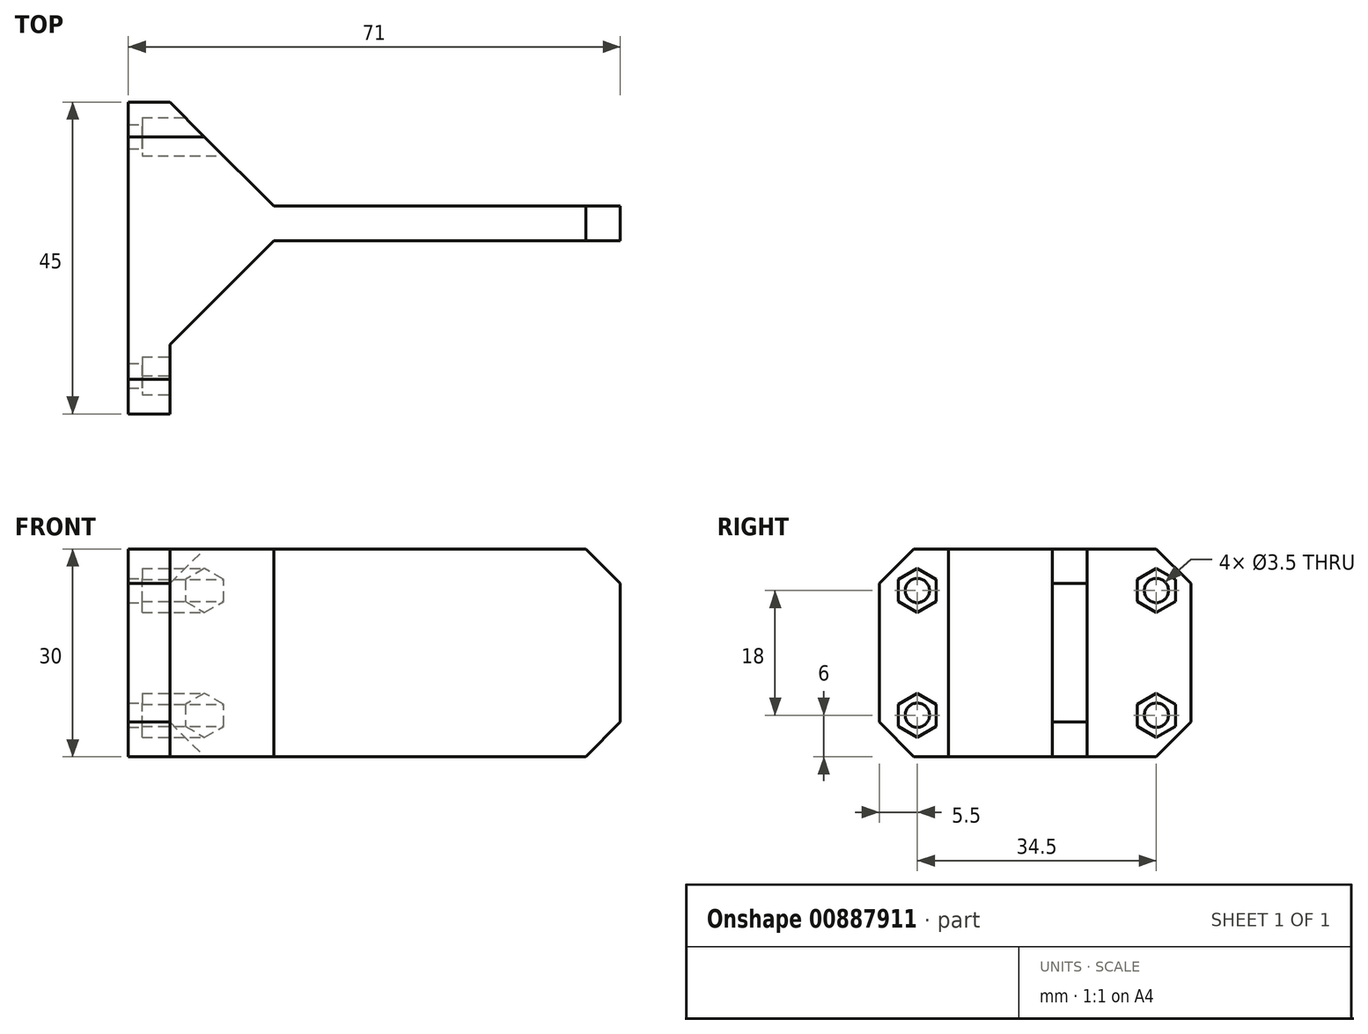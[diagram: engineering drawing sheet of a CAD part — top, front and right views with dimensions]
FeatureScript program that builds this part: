
annotation { "Feature Type Name" : "Feature", "Feature Type Description" : "" }
export const myFeature = defineFeature(function(context is Context, id is Id, definition is map)
    precondition{}
    {
        {
            var Q0;
            Q0=qCreatedBy(makeId("Top.planeOp"),FACE);
            var sketch = newSketch(context, id + "F0", { "sketchPlane" : qUnion([Q0])});
            skLineSegment(sketch, "E0.bottom", {"start": v(0, 0) * mm, "end": v(-6, 0) * mm});
            skLineSegment(sketch, "E0.top", {"start": v(0, 20) * mm, "end": v(-6, 20) * mm});
            skLineSegment(sketch, "E0.left", {"start": v(0, 0) * mm, "end": v(0, 20) * mm});
            skLineSegment(sketch, "E0.right", {"start": v(-6, 0) * mm, "end": v(-6, 20) * mm});
            skLineSegment(sketch, "E1.bottom", {"start": v(0, 0) * mm, "end": v(65, 0) * mm});
            skLineSegment(sketch, "E1.top", {"start": v(0, 5) * mm, "end": v(65, 5) * mm});
            skLineSegment(sketch, "E1.left", {"start": v(0, 0) * mm, "end": v(0, 5) * mm});
            skLineSegment(sketch, "E1.right", {"start": v(65, 0) * mm, "end": v(65, 5) * mm});
            skLineSegment(sketch, "E2.top", {"start": v(0, -25) * mm, "end": v(-6, -25) * mm});
            skLineSegment(sketch, "E2.left", {"start": v(0, 0) * mm, "end": v(0, -25) * mm});
            skLineSegment(sketch, "E2.right", {"start": v(-6, 0) * mm, "end": v(-6, -25) * mm});
            skSolve(sketch);
        }
        {
            var Q0;
            Q0=makeQuery(id+"F0.imprint","IMPRINT",FACE,{"disambiguationData":[TD([[makeQuery(id+"F0.imprint","IMPRINT",EDGE,{"derivedFrom":sQuery(id+"F0.wireOp",EDGE,"E0.bottom")}),-1.0]])]});
            var Q1;
            {var subQ0=sQuery(id+"F0.wireOp",EDGE,"E1.bottom");Q1=makeQuery(id+"F0.imprint","IMPRINT",FACE,{"disambiguationData":[TD([[makeQuery(id+"F0.imprint","IMPRINT",EDGE,{"derivedFrom":subQ0}),1.0]])]});}
            var Q2;
            {var subQ1=sQuery(id+"F0.wireOp",EDGE,"E0.bottom");Q2=makeQuery(id+"F0.imprint","IMPRINT",FACE,{"disambiguationData":[TD([[makeQuery(id+"F0.imprint","IMPRINT",EDGE,{"derivedFrom":subQ1}),-1.0]])]});}
            var Q3;
            Q3=makeQuery(id+"F0.imprint","IMPRINT",FACE,{"disambiguationData":[TD([[makeQuery(id+"F0.imprint","IMPRINT",EDGE,{"derivedFrom":sQuery(id+"F0.wireOp",EDGE,"E0.bottom")}),1.0]])]});
            extrude(context, id + "F1", {"entities" : qUnion([Q0, Q1, Q2, Q3]), "depth" : 30 * mm, "offsetDistance" : 25 * mm});
        }
        {
            var Q0;
            Q0=makeQuery(id+"F1.opExtrude","SWEPT_FACE",FACE,{"disambiguationData":[OSD([sQuery(id+"F0.wireOp",EDGE,"E0.left")])]});
            var sketch = newSketch(context, id + "F2", { "sketchPlane" : qUnion([Q0])});
            skCircle(sketch, "E3.cCircle", {"center": v(15, 24) * mm, "radius": 2.75 * mm, "construction": true});
            skLineSegment(sketch, "E3.0", {"start": v(12.25, 22.41) * mm, "end": v(12.25, 25.59) * mm});
            skLineSegment(sketch, "E3.1", {"start": v(12.25, 25.59) * mm, "end": v(15, 27.18) * mm});
            skLineSegment(sketch, "E3.2", {"start": v(15, 27.18) * mm, "end": v(17.75, 25.59) * mm});
            skLineSegment(sketch, "E3.3", {"start": v(17.75, 25.59) * mm, "end": v(17.75, 22.41) * mm});
            skLineSegment(sketch, "E3.4", {"start": v(17.75, 22.41) * mm, "end": v(15, 20.82) * mm});
            skLineSegment(sketch, "E3.5", {"start": v(15, 20.82) * mm, "end": v(12.25, 22.41) * mm});
            skPoint(sketch, "E3.0.midPoint", {"position": v(12.25, 24) * mm});
            skCircle(sketch, "E4.cCircle", {"center": v(15, 6) * mm, "radius": 2.75 * mm, "construction": true});
            skLineSegment(sketch, "E4.0", {"start": v(12.25, 4.41) * mm, "end": v(12.25, 7.59) * mm});
            skLineSegment(sketch, "E4.1", {"start": v(12.25, 7.59) * mm, "end": v(15, 9.18) * mm});
            skLineSegment(sketch, "E4.2", {"start": v(15, 9.18) * mm, "end": v(17.75, 7.59) * mm});
            skLineSegment(sketch, "E4.3", {"start": v(17.75, 7.59) * mm, "end": v(17.75, 4.41) * mm});
            skLineSegment(sketch, "E4.4", {"start": v(17.75, 4.41) * mm, "end": v(15, 2.82) * mm});
            skLineSegment(sketch, "E4.5", {"start": v(15, 2.82) * mm, "end": v(12.25, 4.41) * mm});
            skPoint(sketch, "E4.0.midPoint", {"position": v(12.25, 6) * mm});
            skCircle(sketch, "E5", {"center": v(15, 24) * mm, "radius": 1.75 * mm});
            skCircle(sketch, "E6", {"center": v(15, 6) * mm, "radius": 1.75 * mm});
            skCircle(sketch, "E7.cCircle", {"center": v(-19.5, 24) * mm, "radius": 2.75 * mm, "construction": true});
            skLineSegment(sketch, "E7.0", {"start": v(-22.25, 22.41) * mm, "end": v(-22.25, 25.59) * mm});
            skLineSegment(sketch, "E7.1", {"start": v(-22.25, 25.59) * mm, "end": v(-19.5, 27.18) * mm});
            skLineSegment(sketch, "E7.2", {"start": v(-19.5, 27.18) * mm, "end": v(-16.75, 25.59) * mm});
            skLineSegment(sketch, "E7.3", {"start": v(-16.75, 25.59) * mm, "end": v(-16.75, 22.41) * mm});
            skLineSegment(sketch, "E7.4", {"start": v(-16.75, 22.41) * mm, "end": v(-19.5, 20.82) * mm});
            skLineSegment(sketch, "E7.5", {"start": v(-19.5, 20.82) * mm, "end": v(-22.25, 22.41) * mm});
            skPoint(sketch, "E7.0.midPoint", {"position": v(-22.25, 24) * mm});
            skCircle(sketch, "E8.cCircle", {"center": v(-19.5, 6) * mm, "radius": 2.75 * mm, "construction": true});
            skLineSegment(sketch, "E8.0", {"start": v(-22.25, 4.41) * mm, "end": v(-22.25, 7.59) * mm});
            skLineSegment(sketch, "E8.1", {"start": v(-22.25, 7.59) * mm, "end": v(-19.5, 9.18) * mm});
            skLineSegment(sketch, "E8.2", {"start": v(-19.5, 9.18) * mm, "end": v(-16.75, 7.59) * mm});
            skLineSegment(sketch, "E8.3", {"start": v(-16.75, 7.59) * mm, "end": v(-16.75, 4.41) * mm});
            skLineSegment(sketch, "E8.4", {"start": v(-16.75, 4.41) * mm, "end": v(-19.5, 2.82) * mm});
            skLineSegment(sketch, "E8.5", {"start": v(-19.5, 2.82) * mm, "end": v(-22.25, 4.41) * mm});
            skPoint(sketch, "E8.0.midPoint", {"position": v(-22.25, 6) * mm});
            skCircle(sketch, "E9", {"center": v(-19.5, 24) * mm, "radius": 1.75 * mm});
            skCircle(sketch, "E10", {"center": v(-19.5, 6) * mm, "radius": 1.75 * mm});
            skSolve(sketch);
        }
        {
            var Q0;
            Q0=makeQuery(id+"F2.imprint","IMPRINT",FACE,{"disambiguationData":[TD([[makeQuery(id+"F2.imprint","IMPRINT",EDGE,{"derivedFrom":sQuery(id+"F2.wireOp",EDGE,"E3.0")}),-1.0]])]});
            var Q1;
            Q1=makeQuery(id+"F2.imprint","IMPRINT",FACE,{"disambiguationData":[TD([[makeQuery(id+"F2.imprint","IMPRINT",EDGE,{"derivedFrom":sQuery(id+"F2.wireOp",EDGE,"E4.0")}),-1.0]])]});
            var Q2;
            Q2=makeQuery(id+"F2.imprint","IMPRINT",FACE,{"disambiguationData":[TD([[makeQuery(id+"F2.imprint","IMPRINT",EDGE,{"derivedFrom":sQuery(id+"F2.wireOp",EDGE,"E9")}),1.0]])]});
            var Q3;
            Q3=makeQuery(id+"F2.imprint","IMPRINT",FACE,{"disambiguationData":[TD([[makeQuery(id+"F2.imprint","IMPRINT",EDGE,{"derivedFrom":sQuery(id+"F2.wireOp",EDGE,"E7.0")}),-1.0]])]});
            var Q4;
            Q4=makeQuery(id+"F2.imprint","IMPRINT",FACE,{"disambiguationData":[TD([[makeQuery(id+"F2.imprint","IMPRINT",EDGE,{"derivedFrom":sQuery(id+"F2.wireOp",EDGE,"E8.0")}),-1.0]])]});
            var Q5;
            Q5=makeQuery(id+"F2.imprint","IMPRINT",FACE,{"disambiguationData":[TD([[makeQuery(id+"F2.imprint","IMPRINT",EDGE,{"derivedFrom":sQuery(id+"F2.wireOp",EDGE,"E10")}),1.0]])]});
            extrude(context, id + "F3", {"entities" : qUnion([Q0, Q1, Q2, Q3, Q4, Q5]), "operationType" : NewBodyOperationType.REMOVE, "oppositeDirection" : true, "depth" : 4 * mm, "offsetDistance" : 25 * mm});
        }
        {
            var Q0;
            Q0=makeQuery(id+"F3.boolean.opBoolean","SPLIT",FACE,{"disambiguationData":[TD([makeQuery(id+"F3.opExtrude","SWEPT_FACE",FACE,{"disambiguationData":[OSD([sQuery(id+"F2.wireOp",EDGE,"E5")])]})])],"derivedFrom":makeQuery(id+"F1.opExtrude","SWEPT_FACE",FACE,{"disambiguationData":[OSD([sQuery(id+"F0.wireOp",EDGE,"E0.left")])]})});
            var Q1;
            Q1=makeQuery(id+"F3.boolean.opBoolean","SPLIT",FACE,{"disambiguationData":[TD([makeQuery(id+"F3.opExtrude","SWEPT_FACE",FACE,{"disambiguationData":[OSD([sQuery(id+"F2.wireOp",EDGE,"E6")])]})])],"derivedFrom":makeQuery(id+"F1.opExtrude","SWEPT_FACE",FACE,{"disambiguationData":[OSD([sQuery(id+"F0.wireOp",EDGE,"E0.left")])]})});
            var Q2;
            Q2=makeQuery(id+"F2.imprint","IMPRINT",FACE,{"disambiguationData":[TD([[makeQuery(id+"F2.imprint","IMPRINT",EDGE,{"derivedFrom":sQuery(id+"F2.wireOp",EDGE,"E9")}),1.0]])]});
            var Q3;
            Q3=makeQuery(id+"F2.imprint","IMPRINT",FACE,{"disambiguationData":[TD([[makeQuery(id+"F2.imprint","IMPRINT",EDGE,{"derivedFrom":sQuery(id+"F2.wireOp",EDGE,"E10")}),1.0]])]});
            extrude(context, id + "F4", {"entities" : qUnion([Q0, Q1, Q2, Q3]), "operationType" : NewBodyOperationType.REMOVE, "endBound" : BoundingType.THROUGH_ALL, "oppositeDirection" : true, "depth" : 25 * mm, "offsetDistance" : 25 * mm});
        }
        {
            var Q0;
            Q0=makeQuery(id+"F1.opExtrude","SWEPT_EDGE",EDGE,{"disambiguationData":[OSD([sQuery(id+"F0.wireOp",EDGE,"E0.left"),sQuery(id+"F0.wireOp",EDGE,"E1.top")])]});
            var Q1;
            Q1=makeQuery(id+"F1.opExtrude","SWEPT_EDGE",EDGE,{"disambiguationData":[OSD([sQuery(id+"F0.wireOp",EDGE,"E0.bottom"),sQuery(id+"F0.wireOp",EDGE,"E0.left"),sQuery(id+"F0.wireOp",EDGE,"E1.bottom"),sQuery(id+"F0.wireOp",EDGE,"E2.left")])]});
            chamfer(context, id + "F5", {"entities" : qUnion([Q0, Q1]), "chamferType" : ChamferType.TWO_OFFSETS, "width1" : 15 * mm, "oppositeDirection" : false, "width2" : 15 * mm, "tangentPropagation" : true});
        }
        {
            var Q0;
            Q0=makeQuery(id+"F1.opExtrude","CAP_EDGE",EDGE,{"disambiguationData":[OSD([sQuery(id+"F0.wireOp",EDGE,"E1.right")])],"isStart":false});
            var Q1;
            Q1=makeQuery(id+"F1.opExtrude","CAP_EDGE",EDGE,{"disambiguationData":[OSD([sQuery(id+"F0.wireOp",EDGE,"E1.right")])],"isStart":true});
            var Q2;
            Q2=makeQuery(id+"F1.opExtrude","CAP_EDGE",EDGE,{"disambiguationData":[OSD([sQuery(id+"F0.wireOp",EDGE,"E2.top")])],"isStart":false});
            var Q3;
            Q3=makeQuery(id+"F1.opExtrude","CAP_EDGE",EDGE,{"disambiguationData":[OSD([sQuery(id+"F0.wireOp",EDGE,"E2.top")])],"isStart":true});
            var Q4;
            Q4=makeQuery(id+"F1.opExtrude","CAP_EDGE",EDGE,{"disambiguationData":[OSD([sQuery(id+"F0.wireOp",EDGE,"E0.top")])],"isStart":false});
            var Q5;
            Q5=makeQuery(id+"F1.opExtrude","CAP_EDGE",EDGE,{"disambiguationData":[OSD([sQuery(id+"F0.wireOp",EDGE,"E0.top")])],"isStart":true});
            chamfer(context, id + "F6", {"entities" : qUnion([Q0, Q1, Q2, Q3, Q4, Q5]), "width" : 5 * mm, "tangentPropagation" : true});
        }
    });
